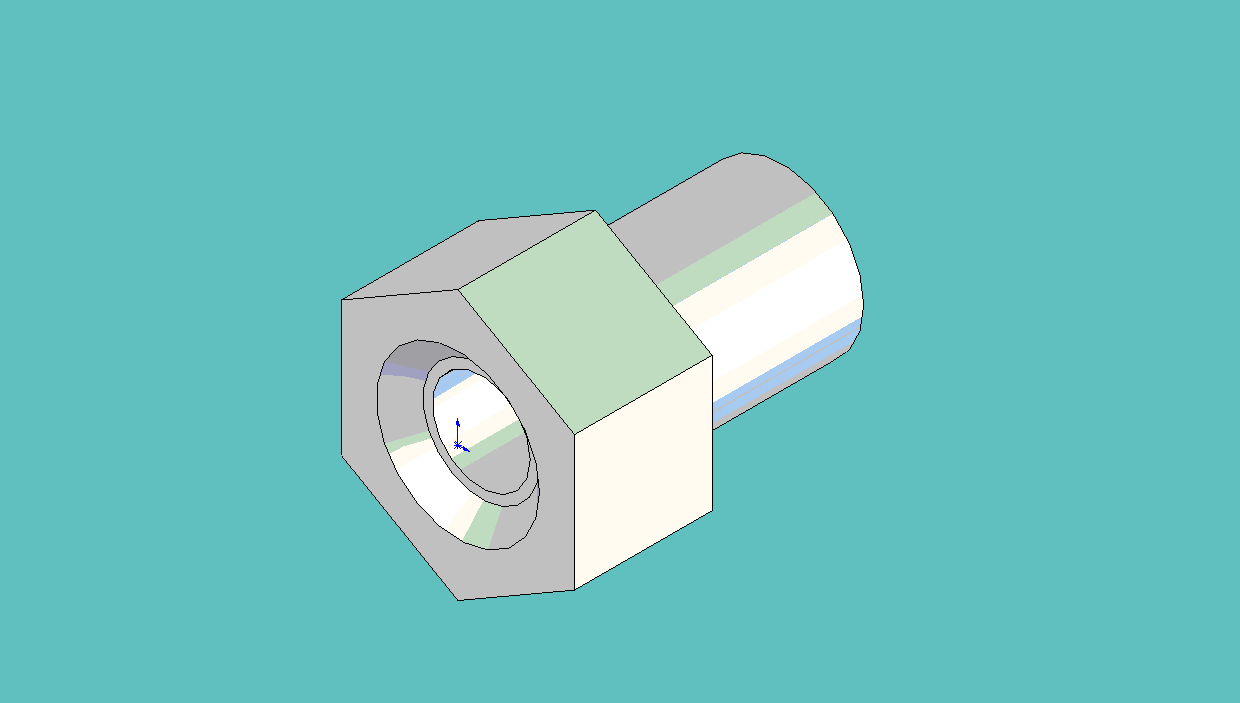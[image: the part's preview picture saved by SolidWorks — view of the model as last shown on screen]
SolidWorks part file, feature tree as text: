
SOLIDWORKS PART (.sldprt)
format: sldprt  version: not decoded by parser v0  size: 168,960 bytes
history: native  units: mm
features: sketch x6, plane x3, extrude x2, cut_extrude x2, material x1, chamfer x1, hole x1, thread x1 (+8 scaffold rows collapsed)
feature tree (25):
  scaffold x8  (default folders/planes/origin — collapsed)
  material  "Matériau <non spécifié>"
  plane  "Plan de face"
  plane  "Plan de dessus"
  plane  "Plan de droite"
  sketch  "Esquisse1"  dims[D1=10.0mm]
  extrude  "Extrusion1"  Depth=5.9mm
  sketch  "Esquisse2"  dims[D1=7.0mm]
  extrude  "Extrusion2"  Depth=8mm
  sketch  "Esquisse3"  dims[D1=5.2mm]
  cut_extrude  "Enlèv. mat.-Extru.1"  Depth=8mm
  sketch  "Esquisse4"  dims[D1=5.0mm]
  cut_extrude  "Enlèv. mat.-Extru.2"  Depth=1mm
  chamfer  "Chanfrein1"  Distance=1mm Angle=45deg
  hole  "Trou taraudé M5x0.81"  Diameter=4.2mm Depth=12.9mm
  sketch  "Esquisse3D2"
  sketch  "Esquisse6"  dims[hole-wizard template sketch: 60 standard entries collapsed; hole parameters kept: c18.Profondeur du trou pour taraudage jusqu'au prochain=12.9mm]
  thread  "Filetage de perçage1"  Diameter=5mm  [1 undecoded]
decode coverage: 12 of 13 modeling features carry decoded parameters
note: ~ marks probable driven/reference dimensions
note: 1 parameter value undecoded
note: suppression state not decoded; provenance and decode notes live in map.json
